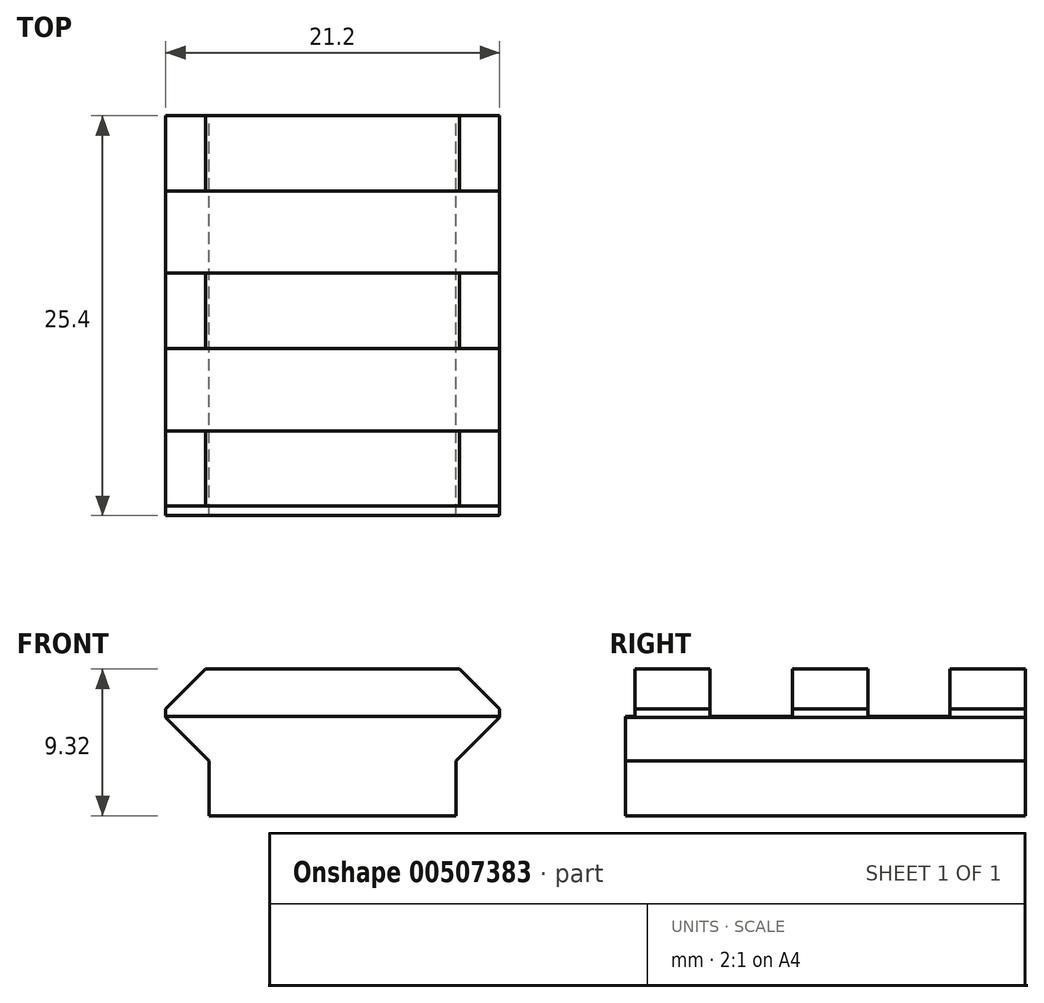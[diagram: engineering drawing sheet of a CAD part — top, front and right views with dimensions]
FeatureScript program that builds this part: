
annotation { "Feature Type Name" : "Feature", "Feature Type Description" : "" }
export const myFeature = defineFeature(function(context is Context, id is Id, definition is map)
    precondition{}
    {
        {
            var Q0;
            Q0=qCreatedBy(makeId("Front.planeOp"),FACE);
            var sketch = newSketch(context, id + "F0", { "sketchPlane" : qUnion([Q0])});
            skLineSegment(sketch, "E0", {"start": v(-7.84, 0) * mm, "end": v(-7.84, 3.5) * mm});
            skLineSegment(sketch, "E1", {"start": v(-7.84, 3.5) * mm, "end": v(-10.6, 6.26) * mm});
            skLineSegment(sketch, "E2", {"start": v(-10.6, 6.26) * mm, "end": v(-10.6, 6.8) * mm});
            skLineSegment(sketch, "E3", {"start": v(-10.6, 6.8) * mm, "end": v(-8.08, 9.32) * mm});
            skLineSegment(sketch, "E4", {"start": v(-8.08, 9.32) * mm, "end": v(8.08, 9.32) * mm});
            skLineSegment(sketch, "E5", {"start": v(8.08, 9.32) * mm, "end": v(10.6, 6.8) * mm});
            skLineSegment(sketch, "E6", {"start": v(10.6, 6.8) * mm, "end": v(10.6, 6.26) * mm});
            skLineSegment(sketch, "E7", {"start": v(10.6, 6.26) * mm, "end": v(7.84, 3.5) * mm});
            skLineSegment(sketch, "E8", {"start": v(7.84, 3.5) * mm, "end": v(7.84, 0) * mm});
            skLineSegment(sketch, "E9.bottom", {"start": v(9.5, 5.16) * mm, "end": v(-9.5, 5.16) * mm, "construction": true});
            skLineSegment(sketch, "E9.top", {"start": v(9.5, 7.9) * mm, "end": v(-9.5, 7.9) * mm, "construction": true});
            skLineSegment(sketch, "E9.left", {"start": v(9.5, 5.16) * mm, "end": v(9.5, 7.9) * mm, "construction": true});
            skLineSegment(sketch, "E9.right", {"start": v(-9.5, 5.16) * mm, "end": v(-9.5, 7.9) * mm, "construction": true});
            skPoint(sketch, "E9.middle", {"position": v(0, 6.53) * mm});
            skLineSegment(sketch, "E10", {"start": v(-7.84, 0) * mm, "end": v(7.84, 0) * mm});
            skSolve(sketch);
        }
        {
            var Q0;
            Q0 = qSketchRegion(id + "F0", true);
            extrude(context, id + "F1", {"entities" : qUnion([Q0]), "depth" : 25.4 * mm});
        }
        {
            var Q0;
            Q0=makeQuery(id+"F1.opExtrude","SWEPT_FACE",FACE,{"disambiguationData":[OSD([sQuery(id+"F0.wireOp",EDGE,"E6")])]});
            var sketch = newSketch(context, id + "F2", { "sketchPlane" : qUnion([Q0])});
            skLineSegment(sketch, "E11", {"start": v(5.23, 9.32) * mm, "end": v(5.23, 6.32) * mm});
            skLineSegment(sketch, "E12", {"start": v(5.23, 6.32) * mm, "end": v(0, 6.32) * mm});
            skLineSegment(sketch, "E13", {"start": v(0, 6.32) * mm, "end": v(0, 9.32) * mm});
            skLineSegment(sketch, "E14", {"start": v(0, 9.32) * mm, "end": v(5.23, 9.32) * mm});
            skLineSegment(sketch, "E15", {"start": v(-4.78, 9.32) * mm, "end": v(-4.78, 6.32) * mm});
            skLineSegment(sketch, "E16", {"start": v(-4.78, 6.32) * mm, "end": v(-10, 6.32) * mm});
            skLineSegment(sketch, "E17", {"start": v(-10, 6.32) * mm, "end": v(-10, 9.32) * mm});
            skLineSegment(sketch, "E18", {"start": v(-10, 9.32) * mm, "end": v(-4.78, 9.32) * mm});
            skPoint(sketch, "E19", {"position": v(-7.4, 9.32) * mm});
            skPoint(sketch, "E20", {"position": v(2.62, 9.32) * mm});
            skLineSegment(sketch, "E21", {"start": v(-14.78, 9.32) * mm, "end": v(-14.78, 6.32) * mm});
            skLineSegment(sketch, "E22", {"start": v(-14.78, 6.32) * mm, "end": v(-20.02, 6.32) * mm});
            skLineSegment(sketch, "E23", {"start": v(-20.02, 6.32) * mm, "end": v(-20.02, 9.32) * mm});
            skLineSegment(sketch, "E24", {"start": v(-20.02, 9.32) * mm, "end": v(-14.78, 9.32) * mm});
            skLineSegment(sketch, "E25", {"start": v(-24.8, 9.32) * mm, "end": v(-24.8, 6.32) * mm});
            skLineSegment(sketch, "E26", {"start": v(-24.8, 6.32) * mm, "end": v(-30.02, 6.32) * mm});
            skLineSegment(sketch, "E27", {"start": v(-30.02, 6.32) * mm, "end": v(-30.02, 9.32) * mm});
            skLineSegment(sketch, "E28", {"start": v(-30.02, 9.32) * mm, "end": v(-24.8, 9.32) * mm});
            skPoint(sketch, "E29", {"position": v(-27.4, 9.32) * mm});
            skPoint(sketch, "E30", {"position": v(-17.4, 9.32) * mm});
            skSolve(sketch);
        }
        {
            var Q0;
            Q0 = qSketchRegion(id + "F2", true);
            extrude(context, id + "F3", {"entities" : qUnion([Q0]), "operationType" : NewBodyOperationType.REMOVE, "endBound" : BoundingType.THROUGH_ALL, "oppositeDirection" : true, "depth" : 25.4 * mm});
        }
    });
